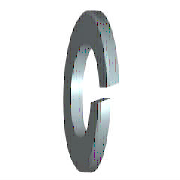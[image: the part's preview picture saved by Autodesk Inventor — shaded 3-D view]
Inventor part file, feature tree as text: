
AUTODESK INVENTOR PART (.ipt)
format: ipt  version: 2021 (Build 250183000, 183)  size: 126,976 bytes
history: native  units: mm (DEFAULTED — no unit token found)
features: sketch x2, extrude x1, other x1, plane x1
ambient origin geometry x6: Origin, YZ Plane, X Axis, Y Axis, Z Axis, Center Point
bodies: Solid1 (feature_tree), Body (feature_tree)
feature tree (5):
  extrude  "Cut"  Depth=18.1mm
  other  "Work Axis1"
  plane  "Work Plane1"
  sketch  "Sketch1"  dims[d0=10.2mm d1=18.1mm]
  sketch  "Sketch2"  dims[d2=2.35mm d3=0.0mm d4=0.47mm d5=0.47mm d6=12.217305mm d7=2.35mm d8=0.0mm d9=0.0mm d10=0.0mm d11=0.0mm d12=0.0mm]
